# Revit family: FantiniCosmi_BIM_CH193WIFI
name_source: partatom
category: Generic Models
units: mm (PartAtom-declared; Revit-internal decimal feet)

## family parameters
Always vertical = Yes
Can host rebar = No
Cut with Voids When Loaded = No
Part Type = Normal
Room Calculation Point = No
Round Connector Dimension = Use Diameter
Shared = No
Work Plane-Based = No

## types (1)
- Standard
    Acoustic signals = buzzer feedback with key pressing
    Adjustable antifreeze temperature range = 2 ÷ 7°C
    Catalog web link = https://www.fantinicosmi.it
    Connection = 3 screw terminals (contact switching NC and NO)
    Default Elevation = 0 mm  [stored 0 ft]
    Description = Pannello remoto LCD per il controllo avanzato di impianti di ventilazione tramite VMC
    Designer = Carniti
    Displayed temperature range = -50 ÷ 50°C
    Electrical insulation = double insulation
    Maximum ambient temperature = 45 °C
    Minimum differential = ±0.1K
    Part Number = Intellitouch CH193WIFI
    Perpetual clock calendar = with backup battery
    Pollution degree = 2
    Power supply = 230V-50Hz
    Prescribed differential = 0,3 K
    Protection degree = IP20
    Pulse voltage = 4000V
    Software Class = A
    Temperature regulation range  = 2 ÷ 40 °C
    Thermal gradient = 4K/h
    Type of action = 1BU (micro disconnection)
    WiFi connection for remote control = through APP Intelliclima+ for Smartphone and Tablet.
    Wireless connection = Wi-Fi 2,4 GHz (802.11 b/g);

note: [stored X ft] marks values corroborated as IEEE doubles in the binary element streams (Revit-internal decimal feet)

## geometry (parser evidence)
native form markers: Sweep x3
no freeform markers — native parametric forms only
